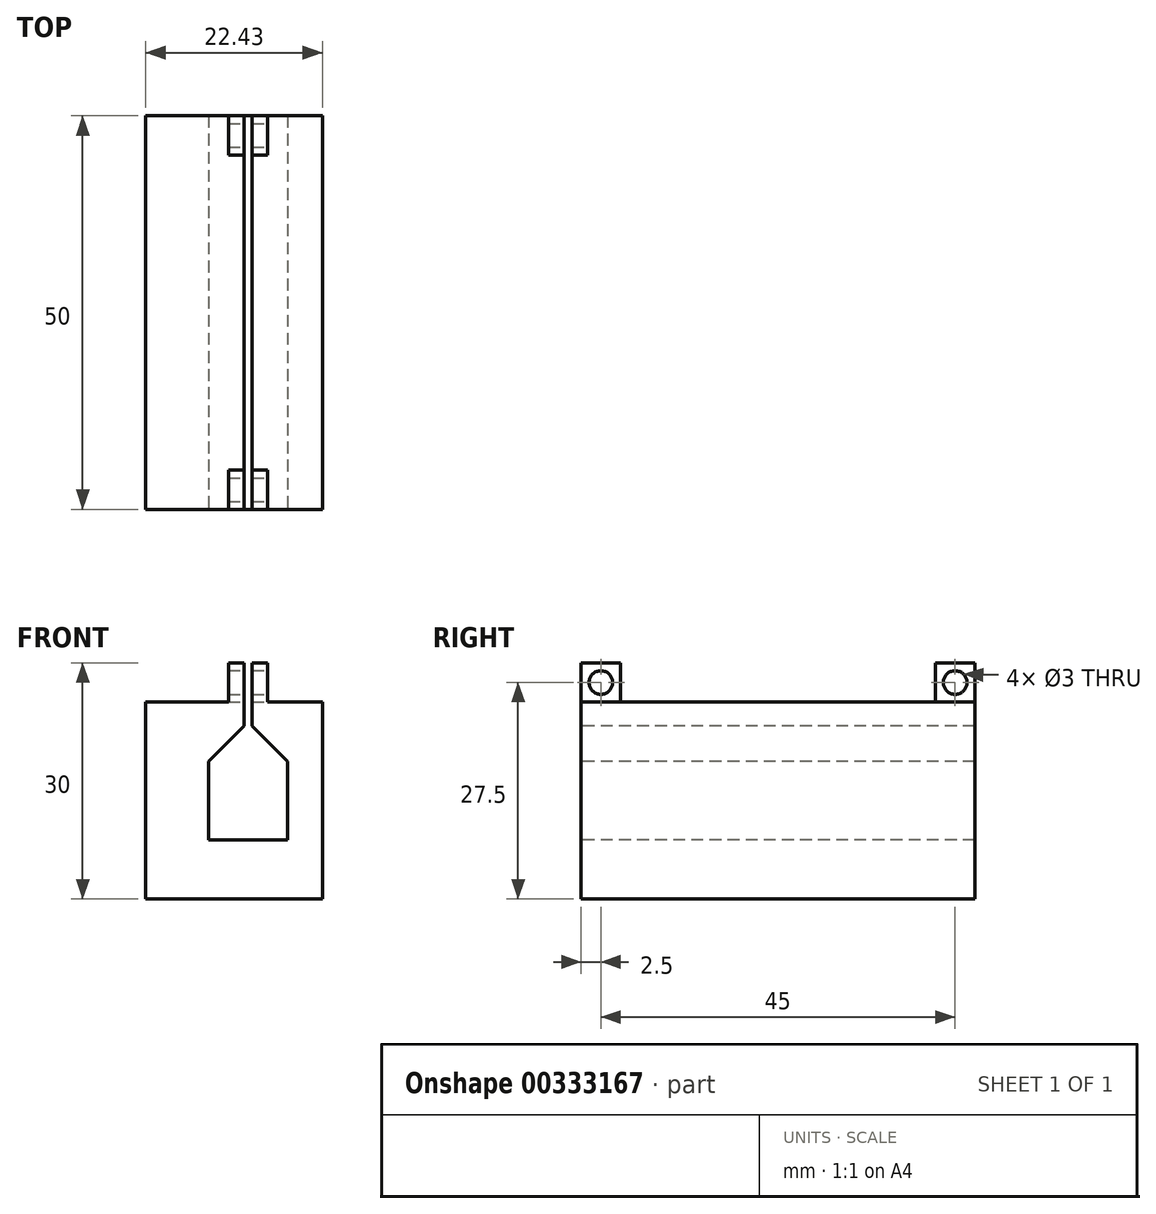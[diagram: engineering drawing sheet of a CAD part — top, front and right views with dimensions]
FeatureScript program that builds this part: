
annotation { "Feature Type Name" : "Feature", "Feature Type Description" : "" }
export const myFeature = defineFeature(function(context is Context, id is Id, definition is map)
    precondition{}
    {
        {
            var Q0;
            Q0=qCreatedBy(makeId("Top.planeOp"),FACE);
            var sketch = newSketch(context, id + "F0", { "sketchPlane" : qUnion([Q0])});
            skLineSegment(sketch, "E0.bottom", {"start": v(13, -25) * mm, "end": v(-13, -25) * mm});
            skLineSegment(sketch, "E0.top", {"start": v(13, 25) * mm, "end": v(-13, 25) * mm});
            skLineSegment(sketch, "E0.left", {"start": v(13, -25) * mm, "end": v(13, 25) * mm});
            skLineSegment(sketch, "E0.right", {"start": v(-13, -25) * mm, "end": v(-13, 25) * mm});
            skPoint(sketch, "E0.middle", {"position": v(0, 0) * mm});
            skSolve(sketch);
        }
        {
            var Q0;
            Q0=makeQuery(id+"F0.imprint","IMPRINT",FACE,{"disambiguationData":[TD([[makeQuery(id+"F0.imprint","IMPRINT",EDGE,{"derivedFrom":sQuery(id+"F0.wireOp",EDGE,"E0.bottom")}),-1.0]])]});
            extrude(context, id + "F1", {"entities" : qUnion([Q0]), "depth" : 25 * mm});
        }
        {
            var Q0;
            Q0=makeQuery(id+"F1.opExtrude","SWEPT_FACE",FACE,{"disambiguationData":[OSD([sQuery(id+"F0.wireOp",EDGE,"E0.bottom")])]});
            var sketch = newSketch(context, id + "F2", { "sketchPlane" : qUnion([Q0])});
            skLineSegment(sketch, "E1.bottom", {"start": v(5, 7.5) * mm, "end": v(-5, 7.5) * mm});
            skLineSegment(sketch, "E1.top", {"start": v(5, 17.5) * mm, "end": v(-5, 17.5) * mm});
            skLineSegment(sketch, "E1.left", {"start": v(5, 7.5) * mm, "end": v(5, 17.5) * mm});
            skLineSegment(sketch, "E1.right", {"start": v(-5, 7.5) * mm, "end": v(-5, 17.5) * mm});
            skPoint(sketch, "E1.middle", {"position": v(0, 12.5) * mm});
            skPoint(sketch, "E1.middle.positionSnap0", {"position": v(13, 12.5) * mm});
            skPoint(sketch, "E1.centerSnap0", {"position": v(13, 12.5) * mm});
            skLineSegment(sketch, "E2", {"start": v(-5, 17.5) * mm, "end": v(-0.5, 22) * mm});
            skLineSegment(sketch, "E3", {"start": v(5, 17.5) * mm, "end": v(0.5, 22) * mm});
            skLineSegment(sketch, "E4", {"start": v(0.5, 17.5) * mm, "end": v(0.5, 33.49) * mm});
            skLineSegment(sketch, "E5", {"start": v(0.5, 33.49) * mm, "end": v(-0.5, 33.49) * mm});
            skLineSegment(sketch, "E6", {"start": v(-0.5, 33.49) * mm, "end": v(-0.5, 17.5) * mm});
            skLineSegment(sketch, "E7", {"start": v(9.43, 25) * mm, "end": v(9.43, 0) * mm});
            skLineSegment(sketch, "E8", {"start": v(9.43, 0) * mm, "end": v(9.43, 2.37) * mm});
            skLineSegment(sketch, "E9", {"start": v(9.43, 2.37) * mm, "end": v(-9.42, 2.37) * mm});
            skLineSegment(sketch, "E10", {"start": v(-9.42, 2.37) * mm, "end": v(-9.42, 25) * mm});
            skSolve(sketch);
        }
        {
            var Q0;
            {var subQ0=sQuery(id+"F0.wireOp",EDGE,"E0.bottom");var subQ1=sQuery(id+"F0.wireOp",EDGE,"E0.right");var subQ2=sQuery(id+"F0.wireOp",EDGE,"E0.top");Q0=makeQuery(id+"F7.boolean.opBoolean","SPLIT",FACE,{"disambiguationData":[TD([makeQuery(id+"F1.opExtrude","SWEPT_FACE",FACE,{"disambiguationData":[OSD([subQ1])]})])],"derivedFrom":makeQuery(id+"F1.opExtrude","CAP_FACE",FACE,{"disambiguationData":[OSD([subQ0,subQ2,sQuery(id+"F0.wireOp",EDGE,"E0.left"),subQ1])],"isStart":false})});}
            var sketch = newSketch(context, id + "F3", { "sketchPlane" : qUnion([Q0])});
            skLineSegment(sketch, "E11.bottom", {"start": v(2.5, -25) * mm, "end": v(-2.5, -25) * mm});
            skLineSegment(sketch, "E11.top", {"start": v(2.5, 25) * mm, "end": v(-2.5, 25) * mm});
            skLineSegment(sketch, "E11.left", {"start": v(2.5, -25) * mm, "end": v(2.5, 25) * mm});
            skLineSegment(sketch, "E11.right", {"start": v(-2.5, -25) * mm, "end": v(-2.5, 25) * mm});
            skPoint(sketch, "E11.middle", {"position": v(0, 0) * mm});
            skSolve(sketch);
        }
        {
            var Q0;
            Q0=qSketchRegion(id+"F3",true);
            extrude(context, id + "F4", {"entities" : qUnion([Q0]), "operationType" : NewBodyOperationType.ADD, "depth" : 5 * mm});
        }
        {
            var Q0;
            Q0=makeQuery(id+"F4.opExtrude","SWEPT_FACE",FACE,{"disambiguationData":[OSD([sQuery(id+"F3.wireOp",EDGE,"E11.left")])]});
            var sketch = newSketch(context, id + "F5", { "sketchPlane" : qUnion([Q0])});
            skCircle(sketch, "E12", {"center": v(-22.5, 27.5) * mm, "radius": 1.5 * mm});
            skPoint(sketch, "E12.centerSnap0", {"position": v(-25, 27.5) * mm});
            skCircle(sketch, "E13", {"center": v(22.5, 27.5) * mm, "radius": 1.5 * mm});
            skPoint(sketch, "E13.centerSnap0", {"position": v(25, 27.5) * mm});
            skSolve(sketch);
        }
        {
            var Q0;
            Q0=makeQuery(id+"F5.imprint","IMPRINT",FACE,{"disambiguationData":[TD([[makeQuery(id+"F5.imprint","IMPRINT",EDGE,{"derivedFrom":sQuery(id+"F5.wireOp",EDGE,"E12")}),1.0]])]});
            var Q1;
            Q1=makeQuery(id+"F5.imprint","IMPRINT",FACE,{"disambiguationData":[TD([[makeQuery(id+"F5.imprint","IMPRINT",EDGE,{"derivedFrom":sQuery(id+"F5.wireOp",EDGE,"E13")}),1.0]])]});
            extrude(context, id + "F6", {"entities" : qUnion([Q0, Q1]), "operationType" : NewBodyOperationType.REMOVE, "oppositeDirection" : true, "depth" : 25 * mm});
        }
        {
            var Q0;
            Q0=makeQuery(id+"F2.imprint","IMPRINT",FACE,{"disambiguationData":[TD([[makeQuery(id+"F2.imprint","IMPRINT",EDGE,{"derivedFrom":sQuery(id+"F2.wireOp",EDGE,"E1.bottom")}),-1.0]])]});
            var Q1;
            {var subQ0=sQuery(id+"F2.wireOp",EDGE,"E3");Q1=makeQuery(id+"F2.imprint","IMPRINT",FACE,{"disambiguationData":[TD([[makeQuery(id+"F2.imprint","IMPRINT",EDGE,{"derivedFrom":subQ0}),1.0]])]});}
            var Q2;
            {var subQ0=sQuery(id+"F2.wireOp",EDGE,"E2");Q2=makeQuery(id+"F2.imprint","IMPRINT",FACE,{"disambiguationData":[TD([[makeQuery(id+"F2.imprint","IMPRINT",EDGE,{"derivedFrom":subQ0}),-1.0]])]});}
            var Q3;
            {var subQ0=sQuery(id+"F2.wireOp",EDGE,"E5");Q3=makeQuery(id+"F2.imprint","IMPRINT",FACE,{"disambiguationData":[TD([[makeQuery(id+"F2.imprint","IMPRINT",EDGE,{"derivedFrom":subQ0}),1.0]])]});}
            var Q4;
            {var subQ0=sQuery(id+"F2.wireOp",EDGE,"E4");var subQ7=sQuery(id+"F2.wireOp",EDGE,"E1.top");var subQ8=makeQuery(id+"F2.imprint","INTERSECT",VERTEX,{"derivedFrom":[subQ7,subQ0]});Q4=makeQuery(id+"F2.imprint","IMPRINT",FACE,{"disambiguationData":[TD([[makeQuery(id+"F2.imprint","IMPRINT",EDGE,{"disambiguationData":[TD([[subQ8,-1.0]])],"derivedFrom":subQ7}),-1.0]])]});}
            var Q5;
            {var subQ4=sQuery(id+"F2.wireOp",EDGE,"E7");Q5=makeQuery(id+"F2.imprint","IMPRINT",FACE,{"disambiguationData":[TD([[makeQuery(id+"F2.imprint","IMPRINT",EDGE,{"derivedFrom":subQ4}),1.0]])]});}
            var Q6;
            {var subQ3=sQuery(id+"F2.wireOp",EDGE,"E8");Q6=makeQuery(id+"F2.imprint","IMPRINT",FACE,{"disambiguationData":[TD([[makeQuery(id+"F2.imprint","IMPRINT",EDGE,{"derivedFrom":subQ3}),1.0]])]});}
            extrude(context, id + "F7", {"entities" : qUnion([Q0, Q1, Q2, Q3, Q4, Q5, Q6]), "operationType" : NewBodyOperationType.REMOVE, "oppositeDirection" : true, "depth" : 77.6 * mm});
        }
        {
            var Q0;
            Q0=makeQuery(id+"F4.opExtrude","SWEPT_FACE",FACE,{"disambiguationData":[OSD([sQuery(id+"F3.wireOp",EDGE,"E11.left")])]});
            var sketch = newSketch(context, id + "F8", { "sketchPlane" : qUnion([Q0])});
            skLineSegment(sketch, "E14", {"start": v(-20, 25) * mm, "end": v(-20, 30) * mm});
            skLineSegment(sketch, "E15", {"start": v(-20, 30) * mm, "end": v(20, 30) * mm});
            skLineSegment(sketch, "E16", {"start": v(20, 30) * mm, "end": v(20, 25) * mm});
            skLineSegment(sketch, "E17", {"start": v(20, 25) * mm, "end": v(-20, 25) * mm});
            skSolve(sketch);
        }
        {
            var Q0;
            Q0=qSketchRegion(id+"F8",true);
            extrude(context, id + "F9", {"entities" : qUnion([Q0]), "operationType" : NewBodyOperationType.REMOVE, "oppositeDirection" : true, "depth" : 25 * mm});
        }
    });
